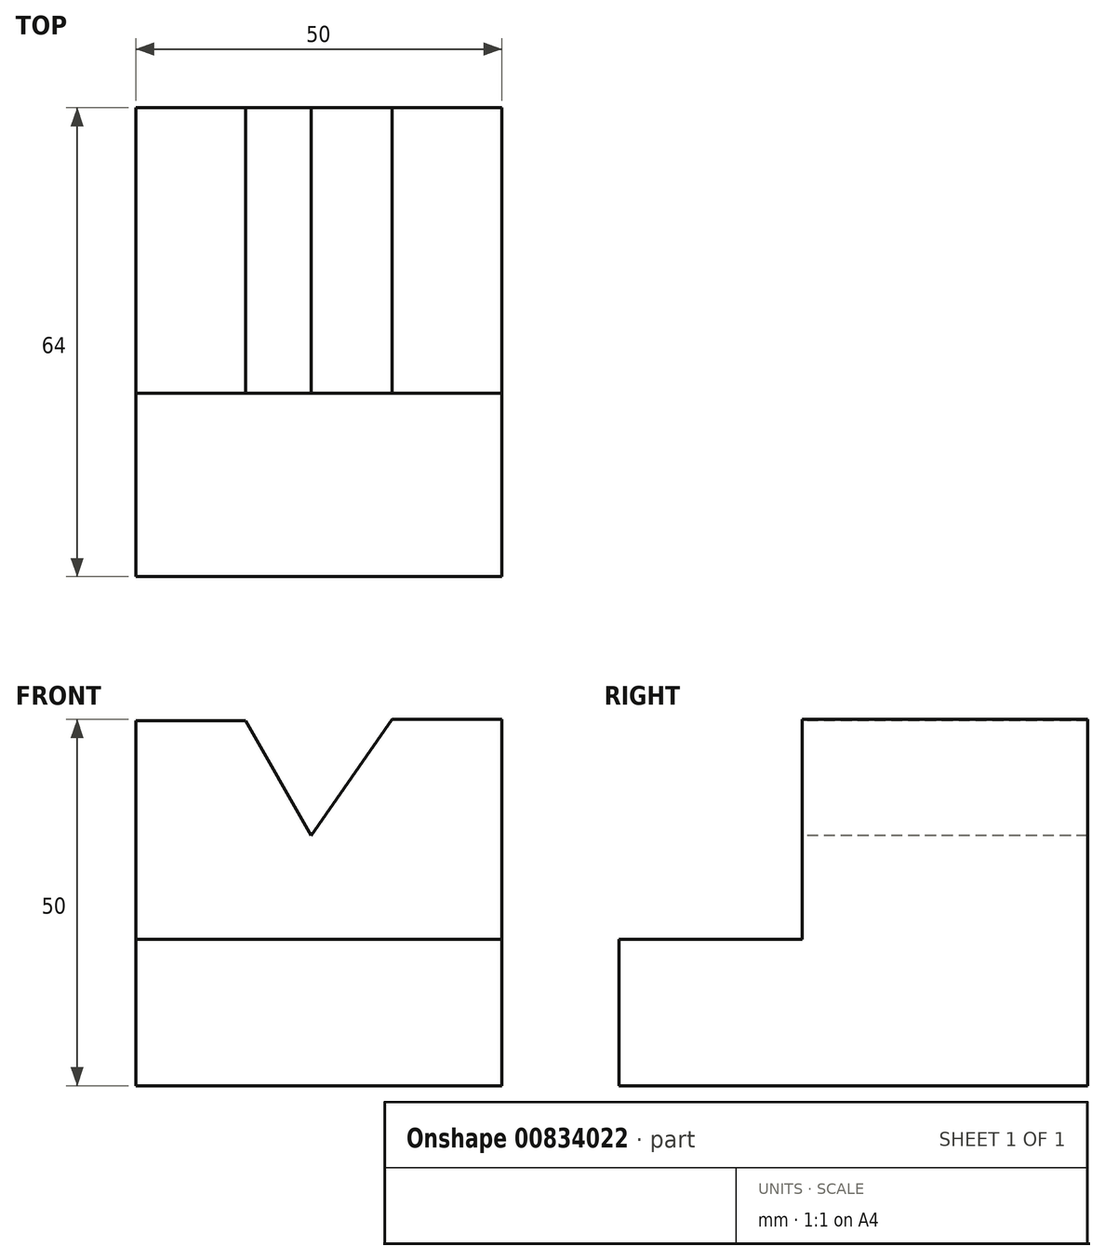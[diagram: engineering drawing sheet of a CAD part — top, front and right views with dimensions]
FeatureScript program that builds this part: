
annotation { "Feature Type Name" : "Feature", "Feature Type Description" : "" }
export const myFeature = defineFeature(function(context is Context, id is Id, definition is map)
    precondition{}
    {
        {
            var Q0;
            Q0=qCreatedBy(makeId("Front.planeOp"),FACE);
            var sketch = newSketch(context, id + "F0", { "sketchPlane" : qUnion([Q0])});
            skLineSegment(sketch, "E0", {"start": v(-32.42, 33.6) * mm, "end": v(-17.42, 33.6) * mm});
            skLineSegment(sketch, "E1", {"start": v(2.58, 33.76) * mm, "end": v(17.58, 33.76) * mm});
            skLineSegment(sketch, "E2", {"start": v(17.58, 33.76) * mm, "end": v(17.58, -16.24) * mm});
            skLineSegment(sketch, "E3", {"start": v(17.58, -16.24) * mm, "end": v(-32.42, -16.24) * mm});
            skLineSegment(sketch, "E4", {"start": v(-32.42, -16.24) * mm, "end": v(-32.42, 33.6) * mm});
            skLineSegment(sketch, "E5", {"start": v(-17.42, 33.6) * mm, "end": v(-8.44, 17.91) * mm});
            skLineSegment(sketch, "E6", {"start": v(-8.44, 17.91) * mm, "end": v(2.58, 33.76) * mm});
            skSolve(sketch);
        }
        {
            var Q0;
            Q0=makeQuery(id+"F0.imprint","IMPRINT",FACE,{"disambiguationData":[TD([[makeQuery(id+"F0.imprint","IMPRINT",EDGE,{"derivedFrom":sQuery(id+"F0.wireOp",EDGE,"E0")}),-1.0]])]});
            extrude(context, id + "F1", {"entities" : qUnion([Q0]), "oppositeDirection" : true, "depth" : 39 * mm, "offsetDistance" : 25 * mm});
        }
        {
            var Q0;
            Q0=makeQuery(id+"F1.opExtrude","CAP_FACE",FACE,{"disambiguationData":[OSD([sQuery(id+"F0.wireOp",EDGE,"E0"),sQuery(id+"F0.wireOp",EDGE,"E1"),sQuery(id+"F0.wireOp",EDGE,"E2"),sQuery(id+"F0.wireOp",EDGE,"E3"),sQuery(id+"F0.wireOp",EDGE,"E4"),sQuery(id+"F0.wireOp",EDGE,"E5"),sQuery(id+"F0.wireOp",EDGE,"E6")])],"isStart":true});
            var sketch = newSketch(context, id + "F2", { "sketchPlane" : qUnion([Q0])});
            skLineSegment(sketch, "E7.bottom", {"start": v(-32.42, -16.24) * mm, "end": v(17.58, -16.24) * mm});
            skLineSegment(sketch, "E7.left", {"start": v(-32.42, -16.24) * mm, "end": v(-32.42, 3.76) * mm});
            skLineSegment(sketch, "E8", {"start": v(-32.42, 3.76) * mm, "end": v(17.58, 3.76) * mm});
            skLineSegment(sketch, "E9", {"start": v(17.58, 3.76) * mm, "end": v(17.58, -16.24) * mm});
            skSolve(sketch);
        }
        {
            var Q0;
            Q0=makeQuery(id+"F2.imprint","IMPRINT",FACE,{"disambiguationData":[TD([[makeQuery(id+"F2.imprint","IMPRINT",EDGE,{"derivedFrom":sQuery(id+"F2.wireOp",EDGE,"E7.bottom")}),-1.0]])]});
            extrude(context, id + "F3", {"entities" : qUnion([Q0]), "operationType" : NewBodyOperationType.ADD, "depth" : 25 * mm, "offsetDistance" : 25 * mm});
        }
    });
